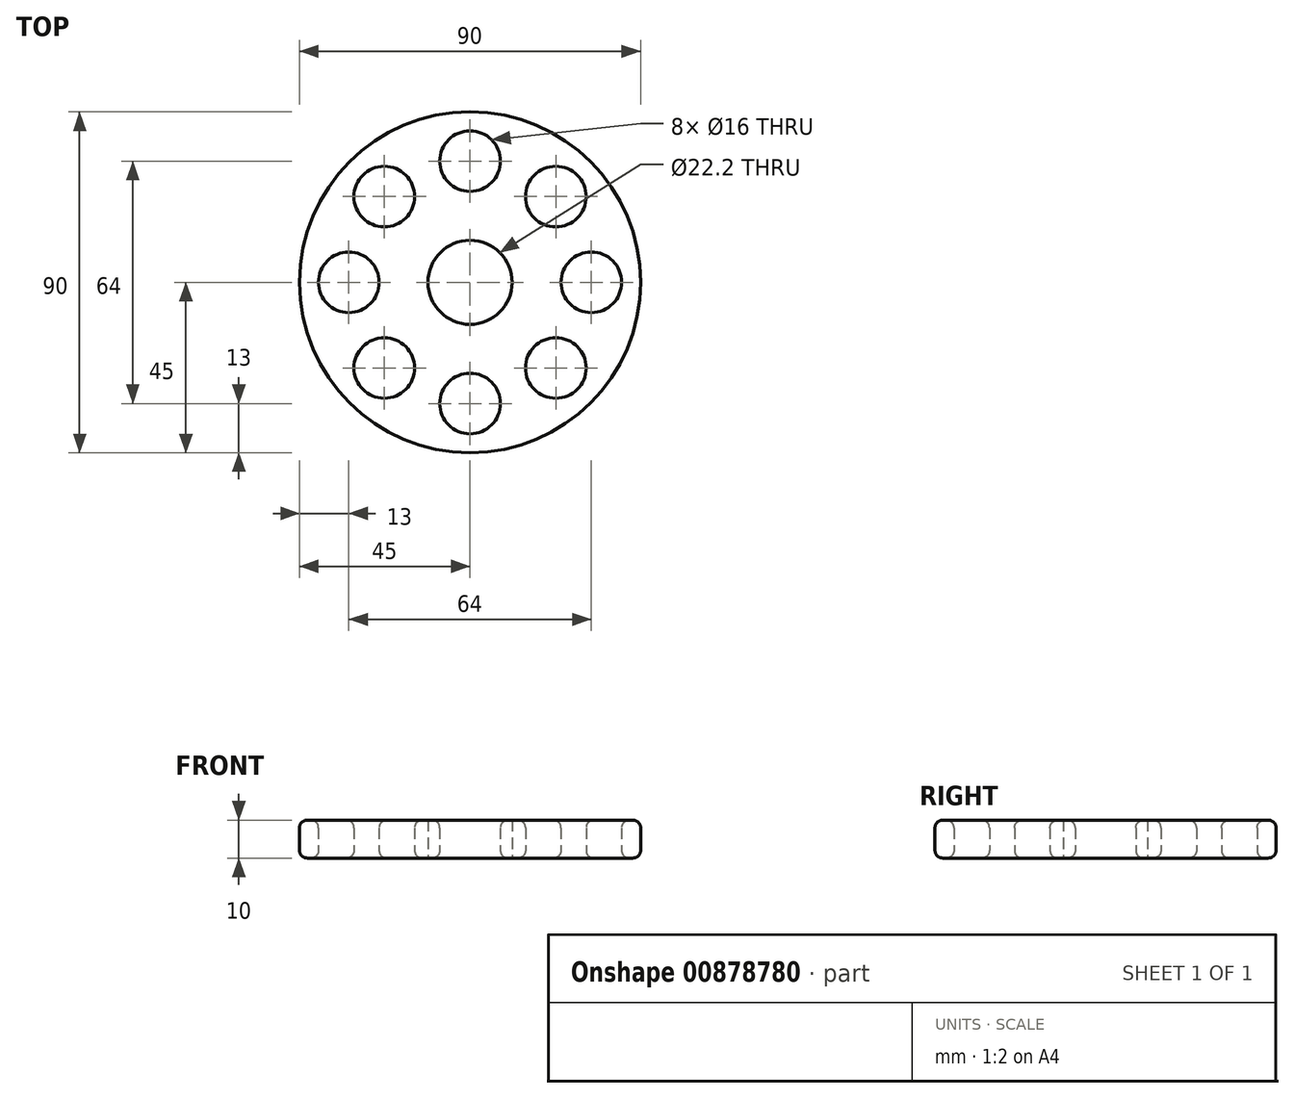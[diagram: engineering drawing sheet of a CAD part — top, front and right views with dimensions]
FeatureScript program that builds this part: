
annotation { "Feature Type Name" : "Feature", "Feature Type Description" : "" }
export const myFeature = defineFeature(function(context is Context, id is Id, definition is map)
    precondition{}
    {
        {
            var Q0;
            Q0=qCreatedBy(makeId("Top.planeOp"),FACE);
            var sketch = newSketch(context, id + "F0", { "sketchPlane" : qUnion([Q0])});
            skCircle(sketch, "E0", {"center": v(0, 0) * mm, "radius": 11.1 * mm});
            skCircle(sketch, "E1", {"center": v(0, 0) * mm, "radius": 45 * mm});
            skCircle(sketch, "E2", {"center": v(32, 0) * mm, "radius": 8 * mm});
            skCircle(sketch, "E3.1.0", {"center": v(22.63, 22.63) * mm, "radius": 8 * mm});
            skCircle(sketch, "E3.2.0", {"center": v(0, 32) * mm, "radius": 8 * mm});
            skCircle(sketch, "E3.3.0", {"center": v(-22.63, 22.63) * mm, "radius": 8 * mm});
            skCircle(sketch, "E3.4.0", {"center": v(-32, 0) * mm, "radius": 8 * mm});
            skCircle(sketch, "E3.5.0", {"center": v(-22.63, -22.63) * mm, "radius": 8 * mm});
            skCircle(sketch, "E3.6.0", {"center": v(0, -32) * mm, "radius": 8 * mm});
            skCircle(sketch, "E3.7.0", {"center": v(22.63, -22.63) * mm, "radius": 8 * mm});
            skSolve(sketch);
        }
        {
            var Q0;
            Q0=makeQuery(id+"F0.imprint","IMPRINT",FACE,{"disambiguationData":[TD([[makeQuery(id+"F0.imprint","IMPRINT",EDGE,{"derivedFrom":sQuery(id+"F0.wireOp",EDGE,"E0")}),-1.0]])]});
            extrude(context, id + "F1", {"entities" : qUnion([Q0]), "depth" : 10 * mm, "offsetDistance" : 25 * mm});
        }
        {
            var Q0;
            Q0=makeQuery(id+"F1.opExtrude","CAP_EDGE",EDGE,{"disambiguationData":[OSD([sQuery(id+"F0.wireOp",EDGE,"E1")])],"isStart":false});
            var Q1;
            Q1=makeQuery(id+"F1.opExtrude","CAP_EDGE",EDGE,{"disambiguationData":[OSD([sQuery(id+"F0.wireOp",EDGE,"E1")])],"isStart":true});
            var Q2;
            Q2=makeQuery(id+"F1.opExtrude","CAP_EDGE",EDGE,{"disambiguationData":[OSD([sQuery(id+"F0.wireOp",EDGE,"E3.2.0")])],"isStart":false});
            var Q3;
            Q3=makeQuery(id+"F1.opExtrude","CAP_EDGE",EDGE,{"disambiguationData":[OSD([sQuery(id+"F0.wireOp",EDGE,"E3.1.0")])],"isStart":false});
            var Q4;
            Q4=makeQuery(id+"F1.opExtrude","CAP_EDGE",EDGE,{"disambiguationData":[OSD([sQuery(id+"F0.wireOp",EDGE,"E2")])],"isStart":false});
            var Q5;
            Q5=makeQuery(id+"F1.opExtrude","CAP_EDGE",EDGE,{"disambiguationData":[OSD([sQuery(id+"F0.wireOp",EDGE,"E3.7.0")])],"isStart":false});
            var Q6;
            Q6=makeQuery(id+"F1.opExtrude","CAP_EDGE",EDGE,{"disambiguationData":[OSD([sQuery(id+"F0.wireOp",EDGE,"E3.6.0")])],"isStart":false});
            var Q7;
            Q7=makeQuery(id+"F1.opExtrude","CAP_EDGE",EDGE,{"disambiguationData":[OSD([sQuery(id+"F0.wireOp",EDGE,"E3.5.0")])],"isStart":false});
            var Q8;
            Q8=makeQuery(id+"F1.opExtrude","CAP_EDGE",EDGE,{"disambiguationData":[OSD([sQuery(id+"F0.wireOp",EDGE,"E3.4.0")])],"isStart":false});
            var Q9;
            Q9=makeQuery(id+"F1.opExtrude","CAP_EDGE",EDGE,{"disambiguationData":[OSD([sQuery(id+"F0.wireOp",EDGE,"E3.3.0")])],"isStart":false});
            var Q10;
            Q10=makeQuery(id+"F1.opExtrude","CAP_EDGE",EDGE,{"disambiguationData":[OSD([sQuery(id+"F0.wireOp",EDGE,"E3.3.0")])],"isStart":true});
            var Q11;
            Q11=makeQuery(id+"F1.opExtrude","CAP_EDGE",EDGE,{"disambiguationData":[OSD([sQuery(id+"F0.wireOp",EDGE,"E3.2.0")])],"isStart":true});
            var Q12;
            Q12=makeQuery(id+"F1.opExtrude","CAP_EDGE",EDGE,{"disambiguationData":[OSD([sQuery(id+"F0.wireOp",EDGE,"E3.1.0")])],"isStart":true});
            var Q13;
            Q13=makeQuery(id+"F1.opExtrude","CAP_EDGE",EDGE,{"disambiguationData":[OSD([sQuery(id+"F0.wireOp",EDGE,"E2")])],"isStart":true});
            var Q14;
            Q14=makeQuery(id+"F1.opExtrude","CAP_EDGE",EDGE,{"disambiguationData":[OSD([sQuery(id+"F0.wireOp",EDGE,"E3.7.0")])],"isStart":true});
            var Q15;
            Q15=makeQuery(id+"F1.opExtrude","CAP_EDGE",EDGE,{"disambiguationData":[OSD([sQuery(id+"F0.wireOp",EDGE,"E3.6.0")])],"isStart":true});
            var Q16;
            Q16=makeQuery(id+"F1.opExtrude","CAP_EDGE",EDGE,{"disambiguationData":[OSD([sQuery(id+"F0.wireOp",EDGE,"E3.5.0")])],"isStart":true});
            var Q17;
            Q17=makeQuery(id+"F1.opExtrude","CAP_EDGE",EDGE,{"disambiguationData":[OSD([sQuery(id+"F0.wireOp",EDGE,"E3.4.0")])],"isStart":true});
            fillet(context, id + "F2", {"entities" : qUnion([Q0, Q1, Q2, Q3, Q4, Q5, Q6, Q7, Q8, Q9, Q10, Q11, Q12, Q13, Q14, Q15, Q16, Q17]), "radius" : 2 * mm, "tangentPropagation" : true, "allowEdgeOverflow" : false});
        }
    });
